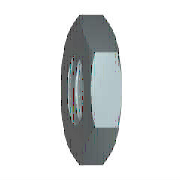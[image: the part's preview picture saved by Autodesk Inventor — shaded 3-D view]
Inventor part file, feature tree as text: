
AUTODESK INVENTOR PART (.ipt)
format: ipt  version: 2015 (Build 190159000, 159)  size: 172,032 bytes
history: native  units: mm (DEFAULTED — no unit token found)
features: sketch x3, chamfer x1, hole x1, other x1, plane x1
ambient origin geometry x7: Origin, YZ Plane, XZ Plane, X Axis, Y Axis, Z Axis, Center Point
bodies: Solid1 (feature_tree), Body (feature_tree)
feature tree (7):
  chamfer  "Chamfer1"  Angle=30.0deg  [1 undecoded]
  hole  "Thread"  [1 undecoded]
  other  "Work Axis1"
  plane  "Work Plane1"
  sketch  "Sketch1"  dims[d0=9.150771mm]
  sketch  "Sketch2"  dims[d1=2.8956mm]
  sketch  "Sketch3"  dims[d2=0.0mm d3=30.0deg d4=30.0deg d5=7.9248mm d6=7.9248mm d7=90.0deg d25=2.6416mm d26=6.0mm d27=4.0mm d28=2.0mm d29=14.3117mm d30=8.0mm d31=20.594885mm d8=0.42963mm d9=30.0deg d10=0.42963mm d11=30.0deg d13=0.0mm d14=0.0mm d39=0.0mm d40=0.42963mm d41=0.42963mm d42=0.0mm]
note: 2 required parameter values undecoded (feature->parameter linkage not recoverable at this tier; creation-order binding heuristic only, values carry confidence <= 0.55)
